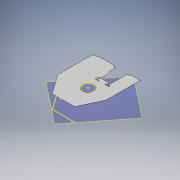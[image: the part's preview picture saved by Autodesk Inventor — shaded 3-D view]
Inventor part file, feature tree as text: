
AUTODESK INVENTOR PART (.ipt)
format: ipt  version: 2018 (Build 220112000, 112)  size: 189,952 bytes
history: native  units: in
note: dims shown in document units (in); Inventor stores cm internally (conversion verified against a paired STEP export)
features: sketch x7, other x5, extrude x3, reference x3, plane x2, hole x1
ambient origin geometry x8: Origin, YZ Plane, XZ Plane, XY Plane, X Axis, Y Axis, Z Axis, Center Point
bodies: Solid1 (feature_tree)
feature tree (21):
  other  "side cover plate Base.ipt"
  hole  "Hole1"  [1 undecoded]
  extrude  "Extrusion1"  Depth=0.0787in TaperAngle=0.0deg
  extrude  "Extrusion2"  [1 undecoded]
  plane  "Work Plane2"
  sketch  "Sketch7"
  extrude  "Extrusion3"  [1 undecoded]
  sketch  "Sketch9"
  other  "Solid1::side cover plate Base.ipt"
  other  "TaggingFeature1"
  sketch  "Sketch4"  dims[d1=6.5in d2=0.75in d3=0.375in d4=0.25in d5=0.5635in d6=1.0in d7=0.8108in d8=1.0in d9=0.0in]
  sketch  "Sketch5"  dims[d10=0.0in d11=0.0in d12=0.0787in d13=0.0in]
  plane  "Work Plane1"
  sketch  "Sketch3"  dims[d0=0.3937in]
  reference  "Reference1"
  sketch  "Sketch6"
  reference  "Reference2"
  reference  "Reference3"
  sketch  "Sketch8"
  other  "Lathe Model 2018.iam"
  other  "BED:1"
note: 3 required parameter values undecoded (feature->parameter linkage not recoverable at this tier; creation-order binding heuristic only, values carry confidence <= 0.55)
